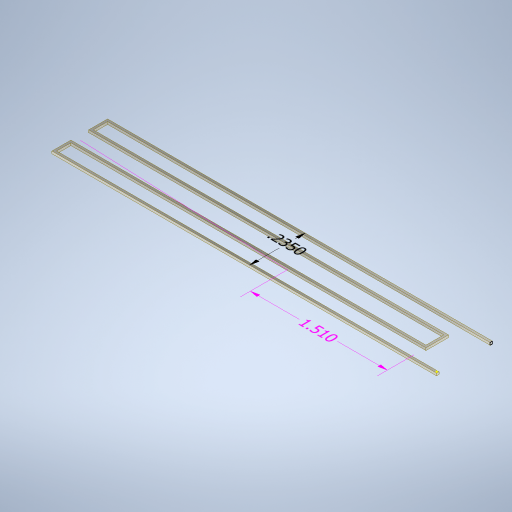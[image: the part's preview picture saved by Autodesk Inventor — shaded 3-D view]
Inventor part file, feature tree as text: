
AUTODESK INVENTOR PART (.ipt)
format: ipt  version: 2024.2 (Build 282272000, 272)  size: 309,760 bytes
history: native  units: in
note: dims shown in document units (in); Inventor stores cm internally (conversion verified against a paired STEP export)
features: sketch x4, other x3, plane x2, sweep x1, extrude x1
ambient origin geometry x8: Origin, YZ Plane, XZ Plane, XY Plane, X Axis, Y Axis, Z Axis, Center Point
bodies: Solid1 (feature_tree)
feature tree (11):
  other  "Annotations"
  sweep  "Sweep1"
  plane  "Work Plane1"
  plane  "Work Plane2"
  sketch  "Sketch10"  dims[d24=0.01in]
  extrude  "Extrusion7"  Depth=0.25in
  sketch  "Sketch1"  dims[d4=0.05in d5=0.05in]
  sketch  "Sketch2"  dims[d6=0.0in d7=0.0in d11=0.25in d19=-0.25in]
  sketch  "Sketch11"  dims[d63=0.01in d65=0.075in d66=0.08in d67=0.08in d69=1.625in d70=1.625in d71=1.0in d72=0.5in d73=0.0in d74=0.0in d42=0.2341in d43=0.169in d44=0.235in d48=0.2141in d49=0.2512in d50=1.51in]
  other  "Linear Dimension 1"
  other  "Linear Dimension 3"
